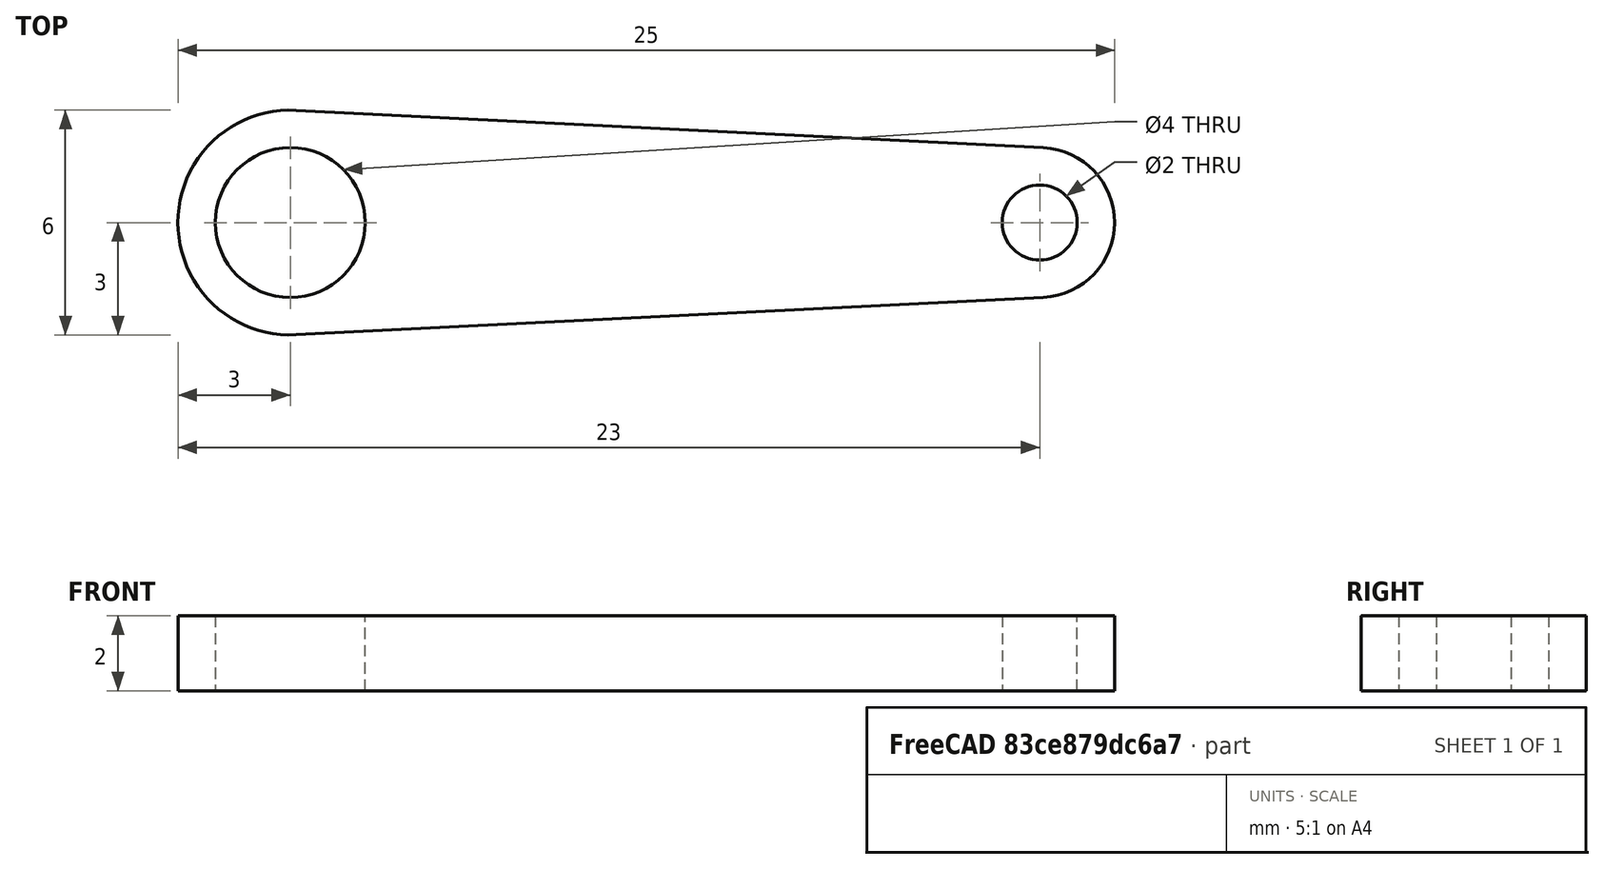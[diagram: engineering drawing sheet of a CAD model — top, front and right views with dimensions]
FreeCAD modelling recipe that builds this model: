
FCSTD DOCUMENT  (FreeCAD 0.18R)
Label: servo-wing
License: All rights reserved
LicenseURL: http://en.wikipedia.org/wiki/All_rights_reserved
objects: Sketcher::SketchObject×1, PartDesign::Pad×1, PartDesign::Body×1
note: 4 computed .brp shape members not serialized (recipe doc carries the construction recipe); baked Part::Feature solids carry a one-line shape summary decoded from their .brp

FEATURE [Sketcher::SketchObject] Sketch
  MapMode = 5
  Support = -> [XY_Plane]
  sketch-geometry (6):
    g0: Circle CenterX=0 CenterY=0 CenterZ=0 NormalX=0 NormalY=0 NormalZ=1 AngleXU=0 Radius=2
    g1: Circle CenterX=20 CenterY=0 CenterZ=0 NormalX=0 NormalY=0 NormalZ=1 AngleXU=0 Radius=1
    g2: LineSegment StartX=0.15 StartY=2.99625 StartZ=0 EndX=20.1 EndY=1.9975 EndZ=0
    g3: LineSegment StartX=0.15 StartY=-2.99625 StartZ=0 EndX=20.1 EndY=-1.9975 EndZ=0
    g4: ArcOfCircle CenterX=0 CenterY=0 CenterZ=0 NormalX=0 NormalY=0 NormalZ=1 AngleXU=0 Radius=3 StartAngle=1.52078 EndAngle=4.76241
    g5: ArcOfCircle CenterX=20 CenterY=0 CenterZ=0 NormalX=0 NormalY=0 NormalZ=1 AngleXU=0 Radius=2 StartAngle=4.76241 EndAngle=7.80396
  constraints (13):
    c: Coincident(g0,g-1)
    c: PointOnObject(g1,g-1)
    c: Radius(g0) = 2
    c: DistanceX(g0,g1) = 20
    c: Radius(g1) = 1
    c: Coincident(g4,g0)
    c: Tangent(g5,g3) = -1.5708
    c: Radius(g5) = 2
    c: Radius(g4) = 3
    c: Tangent(g4,g3) = -1.5708
    c: Coincident(g1,g5)
    c: Tangent(g4,g2) = 1.5708
    c: Tangent(g2,g5) = 1.5708
FEATURE [PartDesign::Pad] Pad
  Length = 2
  Length2 = 100
  Profile = -> Sketch
  Type = 0
FEATURE [PartDesign::Body] Body
  Group = -> [Sketch,Pad]
  Origin = -> Origin
  Tip = -> Pad
